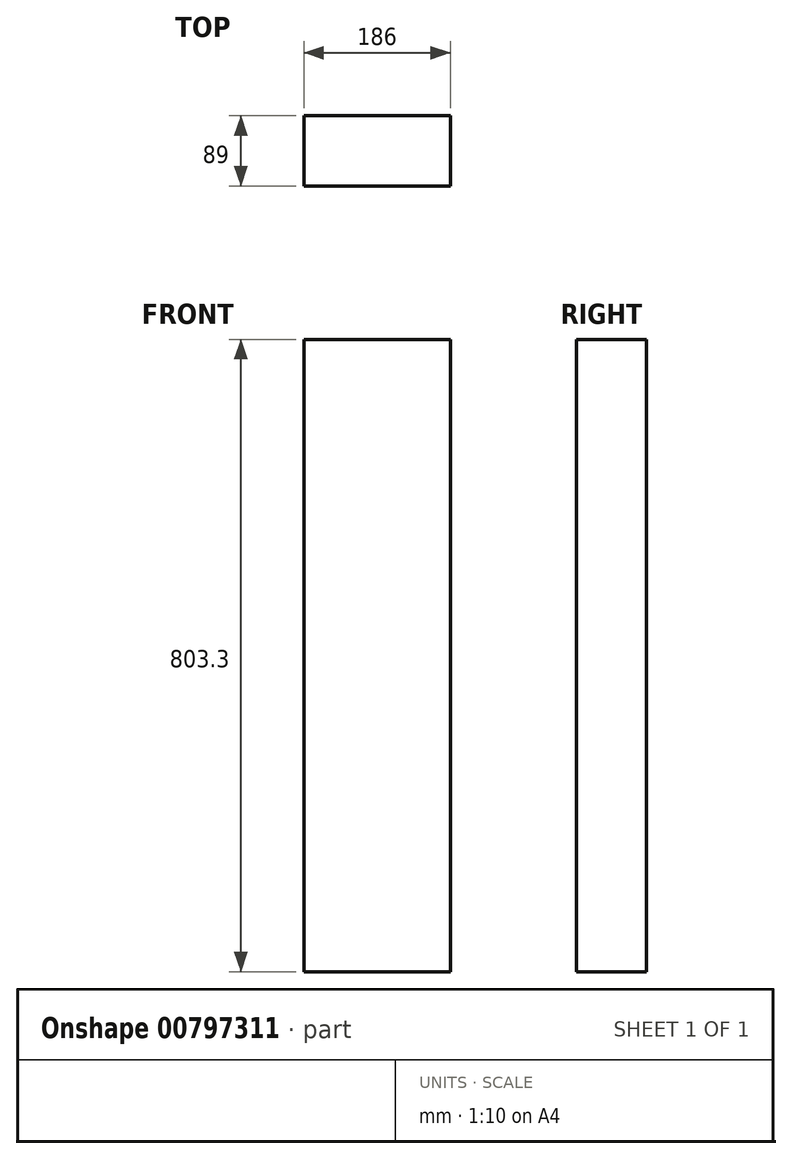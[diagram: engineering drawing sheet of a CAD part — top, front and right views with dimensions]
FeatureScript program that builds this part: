
annotation { "Feature Type Name" : "Feature", "Feature Type Description" : "" }
export const myFeature = defineFeature(function(context is Context, id is Id, definition is map)
    precondition{}
    {
        {
            var Q0;
            Q0=qCreatedBy(makeId("Front.planeOp"),FACE);
            var sketch = newSketch(context, id + "F0", { "sketchPlane" : qUnion([Q0])});
            skLineSegment(sketch, "E0.bottom", {"start": v(93, 401.65) * mm, "end": v(-93, 401.65) * mm});
            skLineSegment(sketch, "E0.top", {"start": v(93, -401.65) * mm, "end": v(-93, -401.65) * mm});
            skLineSegment(sketch, "E0.left", {"start": v(93, 401.65) * mm, "end": v(93, -401.65) * mm});
            skLineSegment(sketch, "E0.right", {"start": v(-93, 401.65) * mm, "end": v(-93, -401.65) * mm});
            skPoint(sketch, "E0.middle", {"position": v(0, 0) * mm});
            skSolve(sketch);
        }
        {
            var Q0;
            Q0=qSketchRegion(id+"F0",true);
            extrude(context, id + "F1", {"entities" : qUnion([Q0]), "depth" : 89 * mm, "offsetDistance" : 25 * mm, "symmetric" : true});
        }
    });
